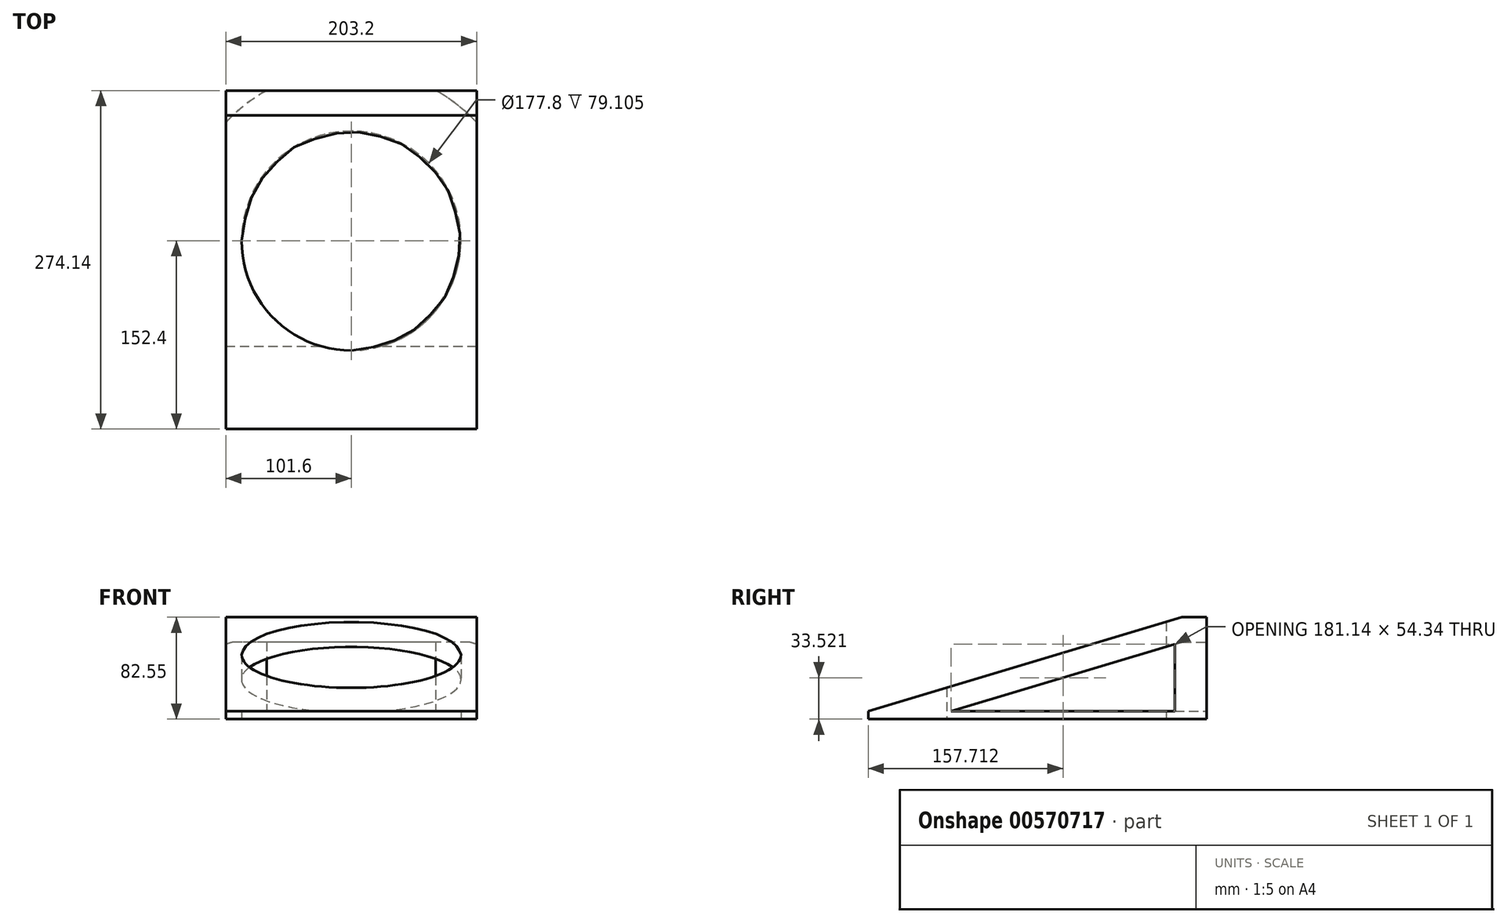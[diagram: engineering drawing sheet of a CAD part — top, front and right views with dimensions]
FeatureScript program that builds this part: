
annotation { "Feature Type Name" : "Feature", "Feature Type Description" : "" }
export const myFeature = defineFeature(function(context is Context, id is Id, definition is map)
    precondition{}
    {
        {
            var Q0;
            Q0=qCreatedBy(makeId("Right.planeOp"),FACE);
            var sketch = newSketch(context, id + "F0", { "sketchPlane" : qUnion([Q0])});
            skLineSegment(sketch, "E0", {"start": v(0, 0) * mm, "end": v(-254, 0) * mm});
            skLineSegment(sketch, "E1", {"start": v(-254, 0) * mm, "end": v(0, 76.2) * mm});
            skLineSegment(sketch, "E2", {"start": v(0, 76.2) * mm, "end": v(0, 0) * mm});
            skSolve(sketch);
        }
        {
            var Q0;
            Q0 = qSketchRegion(id + "F0", true);
            extrude(context, id + "F1", {"entities" : qUnion([Q0]), "endBound" : BoundingType.SYMMETRIC, "depth" : 203.2 * mm, "offsetDistance" : 25.4 * mm});
        }
        {
            var Q0;
            Q0=makeQuery(id+"F1.opExtrude","SWEPT_FACE",FACE,{"disambiguationData":[OSD([sQuery(id+"F0.wireOp",EDGE,"E2")])]});
            var sketch = newSketch(context, id + "F2", { "sketchPlane" : qUnion([Q0])});
            skLineSegment(sketch, "E3.bottom", {"start": v(-101.6, 0) * mm, "end": v(101.6, 0) * mm});
            skLineSegment(sketch, "E3.top", {"start": v(-101.6, 76.2) * mm, "end": v(101.6, 76.2) * mm});
            skLineSegment(sketch, "E3.left", {"start": v(-101.6, 0) * mm, "end": v(-101.6, 76.2) * mm});
            skLineSegment(sketch, "E3.right", {"start": v(101.6, 0) * mm, "end": v(101.6, 76.2) * mm});
            skSolve(sketch);
        }
        {
            var Q0;
            Q0 = qSketchRegion(id + "F2", true);
            extrude(context, id + "F3", {"entities" : qUnion([Q0]), "operationType" : NewBodyOperationType.ADD, "depth" : 20.14 * mm, "offsetDistance" : 25.4 * mm});
        }
        {
            var Q0;
            Q0=makeQuery(id+"F3.boolean.opBoolean","MERGE",FACE,{"derivedFrom":[makeQuery(id+"F1.opExtrude","SWEPT_FACE",FACE,{"disambiguationData":[OSD([sQuery(id+"F0.wireOp",EDGE,"E0")])]}),makeQuery(id+"F3.opExtrude","SWEPT_FACE",FACE,{"disambiguationData":[OSD([sQuery(id+"F2.wireOp",EDGE,"E3.bottom")])]})]});
            var sketch = newSketch(context, id + "F4", { "sketchPlane" : qUnion([Q0])});
            skLineSegment(sketch, "E4.bottom", {"start": v(-101.6, 254) * mm, "end": v(101.6, 254) * mm});
            skLineSegment(sketch, "E4.top", {"start": v(-101.6, -20.14) * mm, "end": v(101.6, -20.14) * mm});
            skLineSegment(sketch, "E4.left", {"start": v(-101.6, 254) * mm, "end": v(-101.6, -20.14) * mm});
            skLineSegment(sketch, "E4.right", {"start": v(101.6, 254) * mm, "end": v(101.6, -20.14) * mm});
            skSolve(sketch);
        }
        {
            var Q0;
            Q0 = qSketchRegion(id + "F4", true);
            extrude(context, id + "F5", {"entities" : qUnion([Q0]), "operationType" : NewBodyOperationType.ADD, "depth" : 6.35 * mm, "offsetDistance" : 25.4 * mm});
        }
        {
            var Q0;
            Q0=qCreatedBy(makeId("Top.planeOp"),FACE);
            var sketch = newSketch(context, id + "F6", { "sketchPlane" : qUnion([Q0])});
            skLineSegment(sketch, "E5", {"start": v(0, 0) * mm, "end": v(0, -101.6) * mm});
            skCircle(sketch, "E6", {"center": v(0, -101.6) * mm, "radius": 139.7 * mm});
            skSolve(sketch);
        }
        {
            var Q0;
            Q0 = qSketchRegion(id + "F6", true);
            extrude(context, id + "F7", {"entities" : qUnion([Q0]), "operationType" : NewBodyOperationType.REMOVE, "endBound" : BoundingType.UP_TO_NEXT, "depth" : 25.4 * mm, "hasOffset" : true, "offsetDistance" : 20.14 * mm});
        }
        {
            var Q0;
            Q0=qCreatedBy(makeId("Top.planeOp"),FACE);
            var sketch = newSketch(context, id + "F8", { "sketchPlane" : qUnion([Q0])});
            skLineSegment(sketch, "E7", {"start": v(0, 0) * mm, "end": v(0, -101.6) * mm});
            skCircle(sketch, "E8", {"center": v(0, -101.6) * mm, "radius": 88.9 * mm});
            skSolve(sketch);
        }
        {
            var Q0;
            Q0 = qSketchRegion(id + "F8", true);
            extrude(context, id + "F9", {"entities" : qUnion([Q0]), "operationType" : NewBodyOperationType.REMOVE, "endBound" : BoundingType.THROUGH_ALL, "depth" : 25.4 * mm, "offsetDistance" : 25.4 * mm, "hasSecondDirection" : true, "secondDirectionBound" : SecondDirectionBoundingType.THROUGH_ALL, "secondDirectionOppositeDirection" : true, "secondDirectionDepth" : 25.4 * mm});
        }
    });
